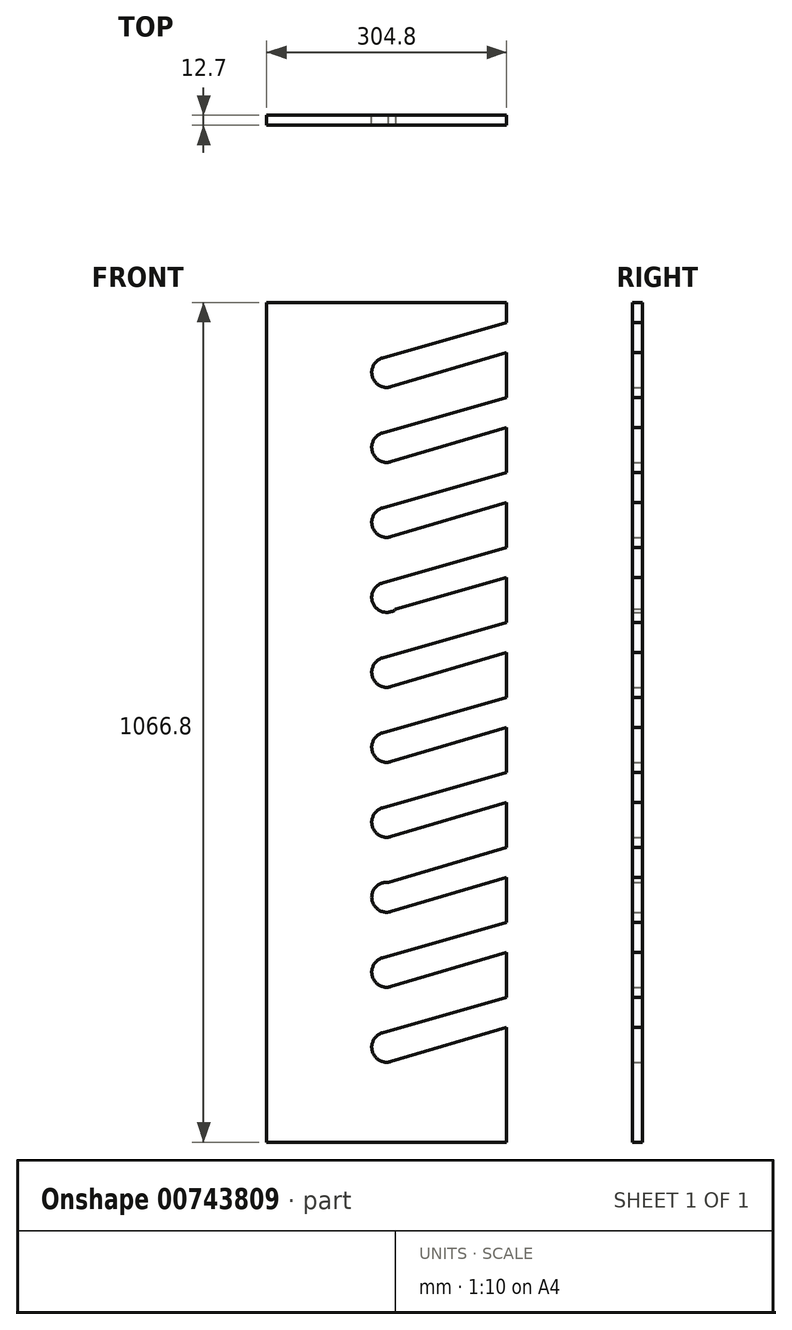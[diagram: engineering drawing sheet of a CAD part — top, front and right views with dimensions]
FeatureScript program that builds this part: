
annotation { "Feature Type Name" : "Feature", "Feature Type Description" : "" }
export const myFeature = defineFeature(function(context is Context, id is Id, definition is map)
    precondition{}
    {
        {
            var Q0;
            Q0=qCreatedBy(makeId("Front.planeOp"),FACE);
            var sketch = newSketch(context, id + "F0", { "sketchPlane" : qUnion([Q0])});
            skLineSegment(sketch, "E0.bottom", {"start": v(152.4, 533.4) * mm, "end": v(-152.4, 533.4) * mm});
            skLineSegment(sketch, "E0.top", {"start": v(152.4, -533.4) * mm, "end": v(-152.4, -533.4) * mm});
            skLineSegment(sketch, "E0.left", {"start": v(152.4, 533.4) * mm, "end": v(152.4, -533.4) * mm});
            skLineSegment(sketch, "E0.right", {"start": v(-152.4, 533.4) * mm, "end": v(-152.4, -533.4) * mm});
            skPoint(sketch, "E0.middle", {"position": v(0, 0) * mm});
            skPoint(sketch, "E1.centerSnap0", {"position": v(0, 533.4) * mm});
            skCircle(sketch, "E2", {"center": v(0, 349.25) * mm, "radius": 19.05 * mm});
            skCircle(sketch, "E3", {"center": v(0, 254) * mm, "radius": 19.05 * mm});
            skCircle(sketch, "E4", {"center": v(0, 158.75) * mm, "radius": 19.05 * mm});
            skCircle(sketch, "E5", {"center": v(0, 63.5) * mm, "radius": 19.05 * mm});
            skCircle(sketch, "E6", {"center": v(0, -31.75) * mm, "radius": 19.05 * mm});
            skCircle(sketch, "E7", {"center": v(0, -127) * mm, "radius": 19.05 * mm});
            skCircle(sketch, "E8", {"center": v(0, -222.25) * mm, "radius": 19.05 * mm});
            skCircle(sketch, "E9", {"center": v(0, -317.5) * mm, "radius": 19.05 * mm});
            skLineSegment(sketch, "E10", {"start": v(152.4, 412.75) * mm, "end": v(-5.25, 367.56) * mm});
            skLineSegment(sketch, "E11", {"start": v(152.4, 374.65) * mm, "end": v(5.42, 330.99) * mm});
            skLineSegment(sketch, "E12", {"start": v(152.4, 317.5) * mm, "end": v(-5.25, 272.31) * mm});
            skLineSegment(sketch, "E13", {"start": v(152.4, 279.4) * mm, "end": v(5.42, 235.74) * mm});
            skLineSegment(sketch, "E14", {"start": v(152.4, 222.25) * mm, "end": v(-5.25, 177.06) * mm});
            skLineSegment(sketch, "E15", {"start": v(152.4, 184.15) * mm, "end": v(-2.22, 139.83) * mm});
            skLineSegment(sketch, "E16", {"start": v(152.4, 127) * mm, "end": v(-5.25, 81.81) * mm});
            skLineSegment(sketch, "E17", {"start": v(152.4, 88.9) * mm, "end": v(5.42, 45.24) * mm});
            skLineSegment(sketch, "E18", {"start": v(152.4, 31.75) * mm, "end": v(-5.25, -13.44) * mm});
            skLineSegment(sketch, "E19", {"start": v(152.4, -6.35) * mm, "end": v(5.42, -50.01) * mm});
            skLineSegment(sketch, "E20", {"start": v(152.4, -63.5) * mm, "end": v(-5.25, -108.69) * mm});
            skLineSegment(sketch, "E21", {"start": v(152.4, -101.6) * mm, "end": v(5.42, -145.26) * mm});
            skLineSegment(sketch, "E22", {"start": v(152.4, -158.75) * mm, "end": v(-12.25, -207.66) * mm});
            skLineSegment(sketch, "E23", {"start": v(152.4, -196.85) * mm, "end": v(5.42, -240.51) * mm});
            skLineSegment(sketch, "E24", {"start": v(152.4, -254) * mm, "end": v(-5.25, -299.19) * mm});
            skLineSegment(sketch, "E25", {"start": v(152.4, -292.1) * mm, "end": v(5.42, -335.76) * mm});
            skCircle(sketch, "E26", {"center": v(0, -412.75) * mm, "radius": 19.05 * mm});
            skLineSegment(sketch, "E27", {"start": v(152.4, -349.25) * mm, "end": v(-5.25, -394.44) * mm});
            skLineSegment(sketch, "E28", {"start": v(152.4, -387.35) * mm, "end": v(5.42, -431.01) * mm});
            skCircle(sketch, "E29.0.1.0", {"center": v(0, 444.5) * mm, "radius": 19.05 * mm});
            skLineSegment(sketch, "E29.0.1.1", {"start": v(152.4, 508) * mm, "end": v(-5.25, 462.81) * mm});
            skLineSegment(sketch, "E29.0.1.2", {"start": v(152.4, 469.9) * mm, "end": v(5.42, 426.24) * mm});
            skLineSegment(sketch, "E29.direction1", {"start": v(0, 349.25) * mm, "end": v(25.4, 349.25) * mm, "construction": true});
            skLineSegment(sketch, "E29.direction2", {"start": v(0, 349.25) * mm, "end": v(0, 444.5) * mm, "construction": true});
            skSolve(sketch);
        }
        {
            var Q0;
            Q0=makeQuery(id+"F0.imprint","IMPRINT",FACE,{"disambiguationData":[TD([[makeQuery(id+"F0.imprint","IMPRINT",EDGE,{"derivedFrom":sQuery(id+"F0.wireOp",EDGE,"E0.bottom")}),1.0]])]});
            extrude(context, id + "F1", {"entities" : qUnion([Q0]), "depth" : 12.7 * mm, "offsetDistance" : 25.4 * mm});
        }
    });
